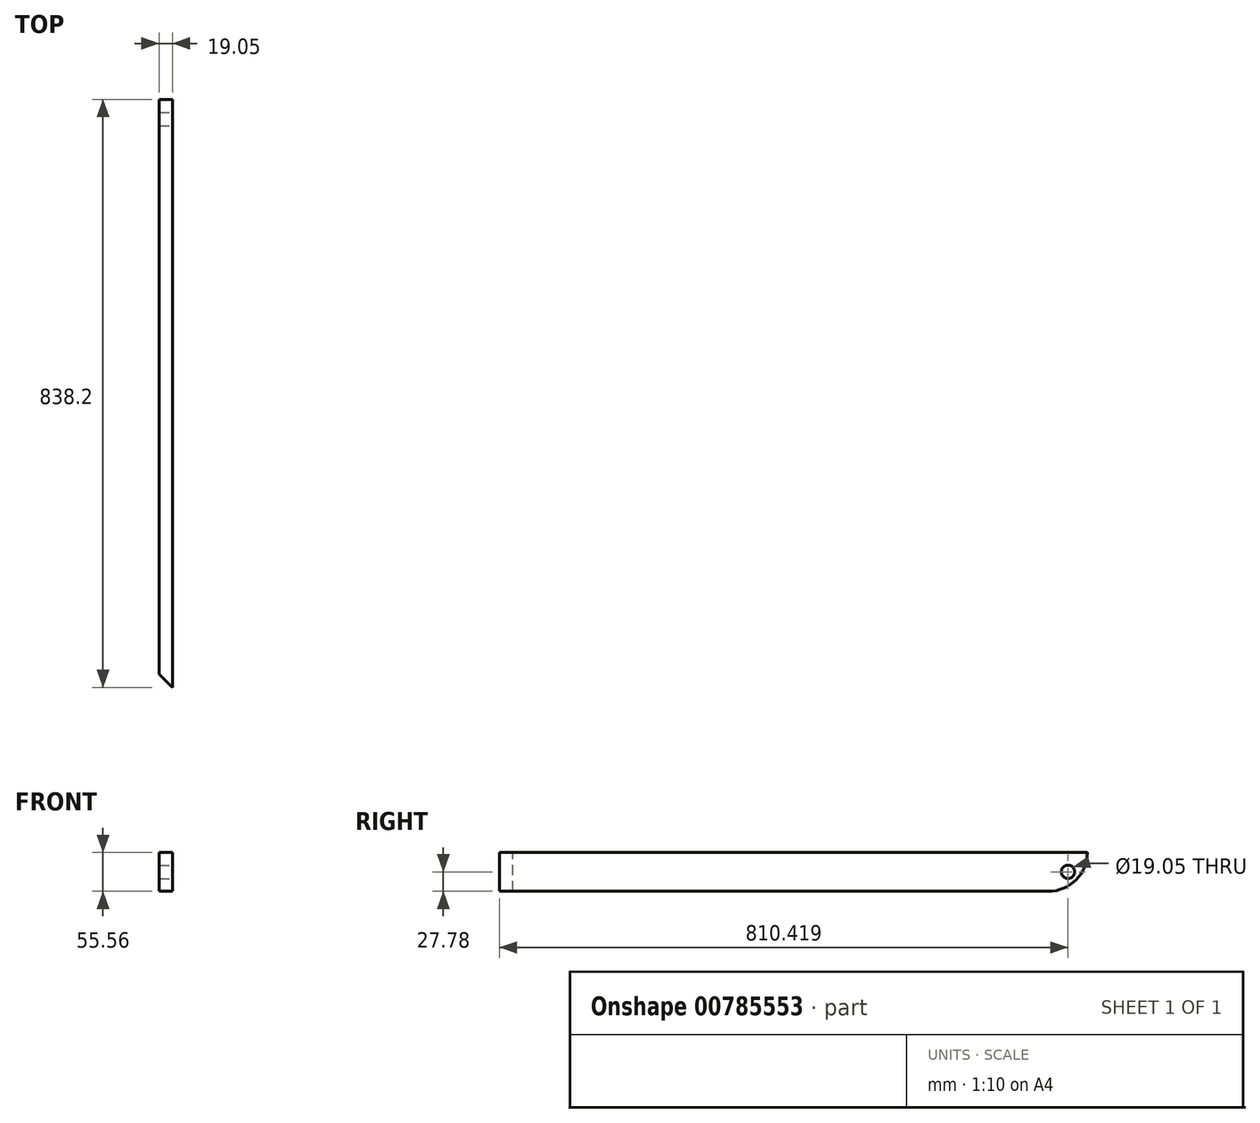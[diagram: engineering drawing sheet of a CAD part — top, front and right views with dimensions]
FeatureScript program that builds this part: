
annotation { "Feature Type Name" : "Feature", "Feature Type Description" : "" }
export const myFeature = defineFeature(function(context is Context, id is Id, definition is map)
    precondition{}
    {
        {
            var Q0;
            Q0=qCreatedBy(makeId("Right.planeOp"),FACE);
            var sketch = newSketch(context, id + "F0", { "sketchPlane" : qUnion([Q0])});
            skLineSegment(sketch, "E0.bottom", {"start": v(419.1, 27.78) * mm, "end": v(-419.1, 27.78) * mm});
            skLineSegment(sketch, "E0.top", {"start": v(419.1, -27.78) * mm, "end": v(-419.1, -27.78) * mm});
            skLineSegment(sketch, "E0.left", {"start": v(419.1, 27.78) * mm, "end": v(419.1, -27.78) * mm});
            skLineSegment(sketch, "E0.right", {"start": v(-419.1, 27.78) * mm, "end": v(-419.1, -27.78) * mm});
            skPoint(sketch, "E0.middle", {"position": v(0, 0) * mm});
            skSolve(sketch);
        }
        {
            var Q0;
            Q0 = qSketchRegion(id + "F0", true);
            extrude(context, id + "F1", {"entities" : qUnion([Q0]), "depth" : 19.05 * mm, "offsetDistance" : 25.4 * mm});
        }
        {
            var Q0;
            Q0=makeQuery(id+"F1.opExtrude","SWEPT_EDGE",EDGE,{"disambiguationData":[OSD([sQuery(id+"F0.wireOp",EDGE,"E0.top"),sQuery(id+"F0.wireOp",EDGE,"E0.left")])]});
            fillet(context, id + "F2", {"entities" : qUnion([Q0]), "radius" : 55.56 * mm, "tangentPropagation" : true, "allowEdgeOverflow" : false});
        }
        {
            var Q0;
            Q0=makeQuery(id+"F1.opExtrude","SWEPT_FACE",FACE,{"disambiguationData":[OSD([sQuery(id+"F0.wireOp",EDGE,"E0.bottom")])]});
            var sketch = newSketch(context, id + "F3", { "sketchPlane" : qUnion([Q0])});
            skLineSegment(sketch, "E1", {"start": v(19.05, -419.1) * mm, "end": v(0, -400.05) * mm});
            skSolve(sketch);
        }
        {
            var Q0;
            Q0 = qSketchRegion(id + "F3", true);
            var Q1;
            {var subQ0=sQuery(id+"F3.wireOp",EDGE,"E1");Q1=makeQuery(id+"F3.imprint","IMPRINT",FACE,{"disambiguationData":[TD([[makeQuery(id+"F3.imprint","IMPRINT",EDGE,{"derivedFrom":subQ0}),1.0]])]});}
            extrude(context, id + "F4", {"entities" : qUnion([Q0, Q1]), "operationType" : NewBodyOperationType.REMOVE, "endBound" : BoundingType.THROUGH_ALL, "oppositeDirection" : true, "depth" : 25.4 * mm, "offsetDistance" : 25.4 * mm});
        }
        {
            var Q0;
            Q0=makeQuery(id+"F1.opExtrude","CAP_FACE",FACE,{"disambiguationData":[OSD([sQuery(id+"F0.wireOp",EDGE,"E0.bottom"),sQuery(id+"F0.wireOp",EDGE,"E0.top"),sQuery(id+"F0.wireOp",EDGE,"E0.left"),sQuery(id+"F0.wireOp",EDGE,"E0.right")])],"isStart":false});
            var sketch = newSketch(context, id + "F5", { "sketchPlane" : qUnion([Q0])});
            skLineSegment(sketch, "E2", {"start": v(419.1, 27.78) * mm, "end": v(363.54, 27.78) * mm});
            skCircle(sketch, "E3", {"center": v(391.32, 0) * mm, "radius": 9.53 * mm});
            skPoint(sketch, "E4.orphan", {"position": v(419.1, -27.78) * mm});
            skSolve(sketch);
        }
        {
            var Q0;
            Q0 = qSketchRegion(id + "F5", true);
            extrude(context, id + "F6", {"entities" : qUnion([Q0]), "operationType" : NewBodyOperationType.REMOVE, "oppositeDirection" : true, "depth" : 25.4 * mm, "offsetDistance" : 25.4 * mm});
        }
    });
